# Revit family: Gira_015900
name_source: partatom
category: Electrical Fixtures
revit_build: Autodesk Revit 2017 (Build: 20160225_1515(x64)
units: mm (PartAtom-declared; Revit-internal decimal feet)

## family parameters
Cut with Voids When Loaded = No
Host = Face
Maintain Annotation Orientation = Yes
Part Type = Normal
Room Calculation Point = No
Round Connector Dimension = Use Diameter
Shared = No

## types (1)
- Wipp-Jal.schalter Einsatz
    Anzahl der Module (bei Modulbauweise) = 1
    Anzahl der Tasten = 2
    Ausführung = Schalter 1-polig
    Available = Yes
    Bedienungsart = Wippe
    Befestigungsart = Krallen-/Schraubbefestigung
    Bemessungsstrom = 10 Ampere
    Category = Jalousieschalter/-taster
    Data sheet (1) = https://katalog.gira.de
    Default Elevation = 1219 mm
    Elektrische und mechanische Verriegelung = Yes
    Elektronisch bedienbar = No
    Farbe = sonstige
    GTIN = 4010337159001
    Geeignet für Schutzart (IP) = IP20
    HAN = 015900
    Halogenfrei = No
    HeinzeBIM = https://bimportal.heinze.de
    Keynote = Einsatz_1fach
    Manufacturer URL = https://www.gira.de
    Mechanisch bedienbar = Yes
    Montageart = unter Putz
    Name = Wipp-Jal.schalter Einsatz
    Nennspannung = 250 Volt
    Oberfläche = sonstige
    Region = DE
    Textfeld/Beschriftungsfläche = No
    Transparent = No
    URL = http://katalog.gira.de
    Werkstoff = sonstige
    Werkstoffgüte = sonstige
    Zusammenstellung = Basiselement

## geometry (parser evidence)
native form markers: Blend x2, Sweep x3
no freeform markers — native parametric forms only
